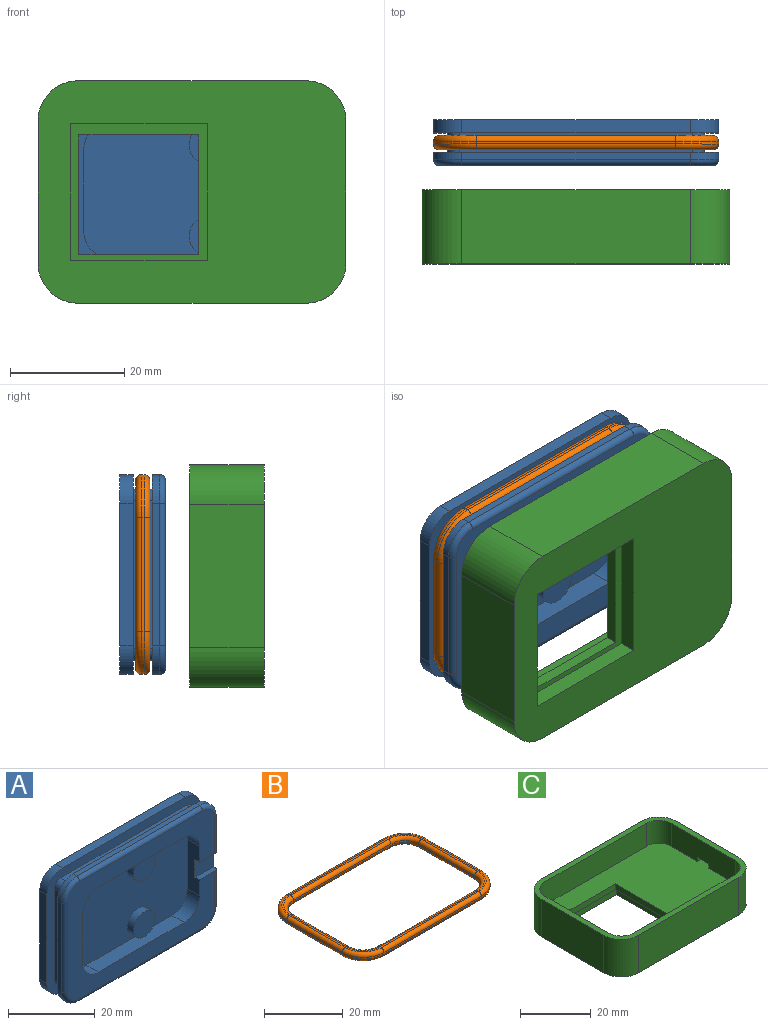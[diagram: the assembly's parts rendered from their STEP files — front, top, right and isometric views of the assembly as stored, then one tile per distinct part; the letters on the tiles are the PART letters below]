
ASSEMBLY  parts=3 mates=2
PART A: 53 faces, bbox 50.8x8x35.8 mm
  f0: plane 41x3.4mm, normal (0,0,-1), area 139.4mm2, adj f25,f26,f49,f52
  f1: plane 25x2.3mm, normal (1,0,0), area 57.5mm2, adj f13,f25,f28,f31
  f2: plane 41x3.4mm, normal (0,0,1), area 139.4mm2, adj f25,f26,f50,f51
  f3: plane 40x2.3mm, normal (0,0,1), area 92mm2, adj f13,f25,f28,f29
  f4: plane 26x3.4mm, normal (-1,0,0), area 88.4mm2, adj f25,f26,f51,f52
  f5: plane 25x2.3mm, normal (-1,0,0), area 57.5mm2, adj f13,f25,f29,f30
  f6: plane 40x2.3mm, normal (0,0,-1), area 92mm2, adj f13,f25,f30,f31
  f7: plane 48x33mm, normal (0,-1,0), area 654.7mm2, adj f8,f14,f15,f16,f22,f23,f32,f33
  f8: plane 14x4mm, normal (-1,0,0), area 48.5mm2, adj f7,f17,f22,f23,f24,f32,f35
  f9: plane 40x1.3mm, normal (0,0,1), area 52mm2, adj f26,f36,f39,f46
  f10: plane 25x1.3mm, normal (-1,0,0), area 32.5mm2, adj f26,f36,f37,f44
  f11: plane 40x1.3mm, normal (0,0,-1), area 52mm2, adj f26,f37,f38,f42
  f12: plane 25x1.3mm, normal (1,0,0), area 30mm2, adj f22,f23,f24,f26,f38,f39,f40,f48
  f13: plane 50x35mm, normal (0,1,0), area 1728.5mm2, adj f1,f3,f5,f6,f28,f29,f30,f31
  f14: plane 28x4mm, normal (0,0,-1), area 112mm2, adj f7,f17,f32,f33
  f15: plane 14x4mm, normal (1,0,0), area 56mm2, adj f7,f17,f33,f34
  f16: plane 28x4mm, normal (0,0,1), area 112mm2, adj f7,f17,f34,f35
  f17: plane 38x24mm, normal (0,-1,0), area 813.6mm2, adj f8,f14,f15,f16,f18,f20,f32,f33
  f18: cylinder r=3.5mm len=7mm, axis (0,1,0), area 44mm2, adj f17,f19
  f19: plane 7x7mm, normal (0,-1,0), area 38.5mm2, adj f18
  f20: cylinder r=3.5mm len=7mm, axis (0,1,0), area 44mm2, adj f17,f21
  f21: plane 7x7mm, normal (0,-1,0), area 38.5mm2, adj f20
  f22: plane 6x1.5mm, normal (0,0,1), area 8.8mm2, adj f7,f8,f12,f24,f40
  f23: plane 6x1.5mm, normal (0,0,-1), area 8.8mm2, adj f7,f8,f12,f24,f48
  f24: plane 6x5mm, normal (0,-1,0), area 30mm2, adj f8,f12,f22,f23
  f25: plane 50x35mm, normal (0,-1,0), area 382mm2, adj f0,f1,f2,f3,f4,f5,f6,f27
  f26: plane 50x35mm, normal (0,1,0), area 382mm2, adj f0,f2,f4,f9,f10,f11,f12,f27
  f27: plane 26x3.4mm, normal (1,0,0), area 88.4mm2, adj f25,f26,f49,f50
  f28: cylinder r=5mm len=5mm, axis (0,1,0), area 18.1mm2, adj f1,f3,f13,f25
  f29: cylinder r=5mm len=5mm, axis (0,1,0), area 18.1mm2, adj f3,f5,f13,f25
  f30: cylinder r=5mm len=5mm, axis (0,1,0), area 18.1mm2, adj f5,f6,f13,f25
  f31: cylinder r=5mm len=5mm, axis (0,1,0), area 18.1mm2, adj f1,f6,f13,f25
  f32: cylinder r=5mm len=5mm, axis (0,-1,0), area 31.4mm2, adj f7,f8,f14,f17
  f33: cylinder r=5mm len=5mm, axis (0,1,0), area 31.4mm2, adj f7,f14,f15,f17
  f34: cylinder r=5mm len=5mm, axis (0,1,0), area 31.4mm2, adj f7,f15,f16,f17
  f35: cylinder r=5mm len=5mm, axis (0,-1,0), area 31.4mm2, adj f7,f8,f16,f17
  f36: cylinder r=5mm len=5mm, axis (0,1,0), area 10.2mm2, adj f9,f10,f26,f45
  f37: cylinder r=5mm len=5mm, axis (0,1,0), area 10.2mm2, adj f10,f11,f26,f43
  f38: cylinder r=5mm len=5mm, axis (0,1,0), area 10.2mm2, adj f11,f12,f26,f41
  f39: cylinder r=5mm len=5mm, axis (0,1,0), area 10.2mm2, adj f9,f12,f26,f47
  f40: cylinder r=1mm len=10mm, axis (0,0,-1), area 15.7mm2, adj f7,f12,f22,f41
  f41: torus R=4mm, axis (0,-1,0), area 11.4mm2, adj f7,f38,f40,f42
  f42: cylinder r=1mm len=40mm, axis (-1,0,0), area 62.8mm2, adj f7,f11,f41,f43
  f43: torus R=4mm, axis (0,-1,0), area 11.4mm2, adj f7,f37,f42,f44
  f44: cylinder r=1mm len=25mm, axis (0,0,1), area 39.3mm2, adj f7,f10,f43,f45
  f45: torus R=4mm, axis (0,-1,0), area 11.4mm2, adj f7,f36,f44,f46
  f46: cylinder r=1mm len=40mm, axis (1,0,0), area 62.8mm2, adj f7,f9,f45,f47
  f47: torus R=4mm, axis (0,-1,0), area 11.4mm2, adj f7,f39,f46,f48
  f48: cylinder r=1mm len=10mm, axis (0,0,-1), area 15.7mm2, adj f7,f12,f23,f47
  f49: cylinder r=2mm len=3.4mm, axis (0,-1,0), area 10.7mm2, adj f0,f25,f26,f27
  f50: cylinder r=2mm len=3.4mm, axis (0,1,0), area 10.7mm2, adj f2,f25,f26,f27
  f51: cylinder r=2mm len=3.4mm, axis (0,1,0), area 10.7mm2, adj f2,f4,f25,f26
  f52: cylinder r=2mm len=3.4mm, axis (0,1,0), area 10.7mm2, adj f0,f4,f25,f26
PART B: 50 faces, bbox 51.2x36.2x2.5 mm
  f0: plane 48x33mm, normal (0,0,1), area 74.6mm2, adj f14,f15,f16,f17,f18,f19,f20,f21
  f1: plane 48x33mm, normal (0,0,-1), area 74.6mm2, adj f22,f23,f24,f25,f26,f27,f28,f29
  f2: plane 35x0.5mm, normal (0,-1,0), area 17.5mm2, adj f30,f34,f45,f48
  f3: plane 20x0.5mm, normal (1,0,0), area 10mm2, adj f31,f35,f42,f45
  f4: plane 35x0.5mm, normal (0,1,0), area 17.5mm2, adj f33,f37,f39,f42
  f5: plane 35x0.5mm, normal (0,-1,0), area 17.5mm2, adj f10,f13,f20,f27
  f6: plane 20x0.5mm, normal (-1,0,0), area 10mm2, adj f10,f11,f16,f23
  f7: plane 35x0.5mm, normal (0,1,0), area 17.5mm2, adj f11,f12,f15,f24
  f8: plane 20x0.5mm, normal (1,0,0), area 10mm2, adj f12,f13,f19,f28
  f9: plane 20x0.5mm, normal (-1,0,0), area 10mm2, adj f32,f36,f39,f48
  f10: cylinder r=5mm len=5mm, axis (0,0,1), area 3.9mm2, adj f5,f6,f18,f25
  f11: cylinder r=5mm len=5mm, axis (0,0,-1), area 3.9mm2, adj f6,f7,f14,f22
  f12: cylinder r=5mm len=5mm, axis (0,0,1), area 3.9mm2, adj f7,f8,f17,f26
  f13: cylinder r=5mm len=5mm, axis (0,0,-1), area 3.9mm2, adj f5,f8,f21,f29
  f14: torus R=6mm, axis (0,0,1), area 13.2mm2, adj f0,f11,f15,f16
  f15: cylinder r=1mm len=35mm, axis (1,0,0), area 55mm2, adj f0,f7,f14,f17
  f16: cylinder r=1mm len=20mm, axis (0,1,0), area 31.4mm2, adj f0,f6,f14,f18
  f17: torus R=6mm, axis (0,0,1), area 13.2mm2, adj f0,f12,f15,f19
  f18: torus R=6mm, axis (0,0,1), area 13.2mm2, adj f0,f10,f16,f20
  f19: cylinder r=1mm len=20mm, axis (0,-1,0), area 31.4mm2, adj f0,f8,f17,f21
  f20: cylinder r=1mm len=35mm, axis (-1,0,0), area 55mm2, adj f0,f5,f18,f21
  f21: torus R=6mm, axis (0,0,1), area 13.2mm2, adj f0,f13,f19,f20
  f22: torus R=6mm, axis (0,0,1), area 13.2mm2, adj f1,f11,f23,f24
  f23: cylinder r=1mm len=20mm, axis (0,-1,0), area 31.4mm2, adj f1,f6,f22,f25
  f24: cylinder r=1mm len=35mm, axis (-1,0,0), area 55mm2, adj f1,f7,f22,f26
  f25: torus R=6mm, axis (0,0,1), area 13.2mm2, adj f1,f10,f23,f27
  f26: torus R=6mm, axis (0,0,1), area 13.2mm2, adj f1,f12,f24,f28
  f27: cylinder r=1mm len=35mm, axis (1,0,0), area 55mm2, adj f1,f5,f25,f29
  f28: cylinder r=1mm len=20mm, axis (0,1,0), area 31.4mm2, adj f1,f8,f26,f29
  f29: torus R=6mm, axis (0,0,1), area 13.2mm2, adj f1,f13,f27,f28
  f30: cylinder r=1mm len=35mm, axis (1,0,0), area 55mm2, adj f1,f2,f46,f49
  f31: cylinder r=1mm len=20mm, axis (0,1,0), area 31.4mm2, adj f1,f3,f43,f46
  f32: cylinder r=1mm len=20mm, axis (0,-1,0), area 31.4mm2, adj f1,f9,f40,f49
  f33: cylinder r=1mm len=35mm, axis (-1,0,0), area 55mm2, adj f1,f4,f40,f43
  f34: cylinder r=1mm len=35mm, axis (-1,0,0), area 55mm2, adj f0,f2,f44,f47
  f35: cylinder r=1mm len=20mm, axis (0,-1,0), area 31.4mm2, adj f0,f3,f41,f44
  f36: cylinder r=1mm len=20mm, axis (0,1,0), area 31.4mm2, adj f0,f9,f38,f47
  f37: cylinder r=1mm len=35mm, axis (1,0,0), area 55mm2, adj f0,f4,f38,f41
  f38: torus R=6.5mm, axis (0,0,1), area 17.6mm2, adj f0,f36,f37,f39
  f39: cylinder r=7.5mm len=7.5mm, axis (0,0,1), area 5.9mm2, adj f4,f9,f38,f40
  f40: torus R=6.5mm, axis (0,0,1), area 17.6mm2, adj f1,f32,f33,f39
  f41: torus R=6.5mm, axis (0,0,1), area 17.6mm2, adj f0,f35,f37,f42
  f42: cylinder r=7.5mm len=7.5mm, axis (0,0,-1), area 5.9mm2, adj f3,f4,f41,f43
  f43: torus R=6.5mm, axis (0,0,1), area 17.6mm2, adj f1,f31,f33,f42
  f44: torus R=6.5mm, axis (0,0,1), area 17.6mm2, adj f0,f34,f35,f45
  f45: cylinder r=7.5mm len=7.5mm, axis (0,0,1), area 5.9mm2, adj f2,f3,f44,f46
  f46: torus R=6.5mm, axis (0,0,1), area 17.6mm2, adj f1,f30,f31,f45
  f47: torus R=6.5mm, axis (0,0,1), area 17.6mm2, adj f0,f34,f36,f48
  f48: cylinder r=7.5mm len=7.5mm, axis (0,0,-1), area 5.9mm2, adj f2,f9,f47,f49
  f49: torus R=6.5mm, axis (0,0,1), area 17.6mm2, adj f1,f30,f32,f48
PART C: 31 faces, bbox 54x39x13 mm
  f0: plane 52.25x35.5mm, normal (0,0,1), area 1338.2mm2, adj f1,f7,f8,f9,f10,f16,f17,f18
  f1: plane 25x13mm, normal (1,0,0), area 318.3mm2, adj f0,f5,f6,f24,f27,f28,f29,f30
  f2: plane 40x13mm, normal (0,1,0), area 520mm2, adj f5,f6,f24,f25
  f3: plane 25x13mm, normal (-1,0,0), area 325mm2, adj f5,f6,f25,f26
  f4: plane 40x13mm, normal (0,-1,0), area 520mm2, adj f5,f6,f26,f27
  f5: plane 54x39mm, normal (0,0,1), area 292.6mm2, adj f1,f2,f3,f4,f7,f8,f9,f10
  f6: plane 54x39mm, normal (0,0,-1), area 1487.9mm2, adj f1,f2,f3,f4,f11,f12,f13,f14
  f7: plane 25.5x8mm, normal (-1,0,0), area 197.2mm2, adj f0,f5,f20,f23,f28,f29,f30
  f8: plane 40.5x8mm, normal (0,-1,0), area 324mm2, adj f0,f5,f20,f21
  f9: plane 25.5x8mm, normal (1,0,0), area 204mm2, adj f0,f5,f21,f22
  f10: plane 40.5x8mm, normal (0,1,0), area 324mm2, adj f0,f5,f22,f23
  f11: plane 24x3mm, normal (1,0,0), area 72mm2, adj f6,f12,f14,f15
  f12: plane 24x3mm, normal (0,-1,0), area 72mm2, adj f6,f11,f13,f15
  f13: plane 24x3mm, normal (-1,0,0), area 72mm2, adj f6,f12,f14,f15
  f14: plane 24x3mm, normal (0,1,0), area 72mm2, adj f6,f11,f13,f15
  f15: plane 24x24mm, normal (0,0,-1), area 135mm2, adj f11,f12,f13,f14,f16,f17,f18,f19
  f16: plane 21x2mm, normal (1,0,0), area 42mm2, adj f0,f15,f17,f19
  f17: plane 21x2mm, normal (0,-1,0), area 42mm2, adj f0,f15,f16,f18
  f18: plane 21x2mm, normal (-1,0,0), area 42mm2, adj f0,f15,f17,f19
  f19: plane 21x2mm, normal (0,1,0), area 42mm2, adj f0,f15,f16,f18
  f20: cylinder r=5mm len=8mm, axis (0,0,-1), area 62.8mm2, adj f0,f5,f7,f8
  f21: cylinder r=5mm len=8mm, axis (0,0,1), area 62.8mm2, adj f0,f5,f8,f9
  f22: cylinder r=5mm len=8mm, axis (0,0,-1), area 62.8mm2, adj f0,f5,f9,f10
  f23: cylinder r=5mm len=8mm, axis (0,0,1), area 62.8mm2, adj f0,f5,f7,f10
  f24: cylinder r=7mm len=13mm, axis (0,0,-1), area 142.9mm2, adj f1,f2,f5,f6
  f25: cylinder r=7mm len=13mm, axis (0,0,1), area 142.9mm2, adj f2,f3,f5,f6
  f26: cylinder r=7mm len=13mm, axis (0,0,-1), area 142.9mm2, adj f3,f4,f5,f6
  f27: cylinder r=7mm len=13mm, axis (0,0,1), area 142.9mm2, adj f1,f4,f5,f6
  f28: plane 1.75x1.5mm, normal (0,1,0), area 2.6mm2, adj f0,f1,f7,f30
  f29: plane 1.75x1.5mm, normal (0,-1,0), area 2.6mm2, adj f0,f1,f7,f30
  f30: plane 4.5x1.75mm, normal (0,0,-1), area 7.9mm2, adj f1,f7,f28,f29
PLACE A t=(-7.38,-52.15,-28.04)mm
PLACE B rot(axis=(1,0,0),90deg) t=(17.62,-54.9,-10.54)mm
PLACE C rot(axis=(-1,0,0),90deg) t=(17.62,-77.42,-10.79)mm
MATE fastened B.f5 <-> A.f2  axis (0,0,-1) through (17.62,-56.15,4.46)mm
MATE slider C.f0 <-> A.f13  axis (0,1,0) through (17.62,-72.42,6.96)mm
